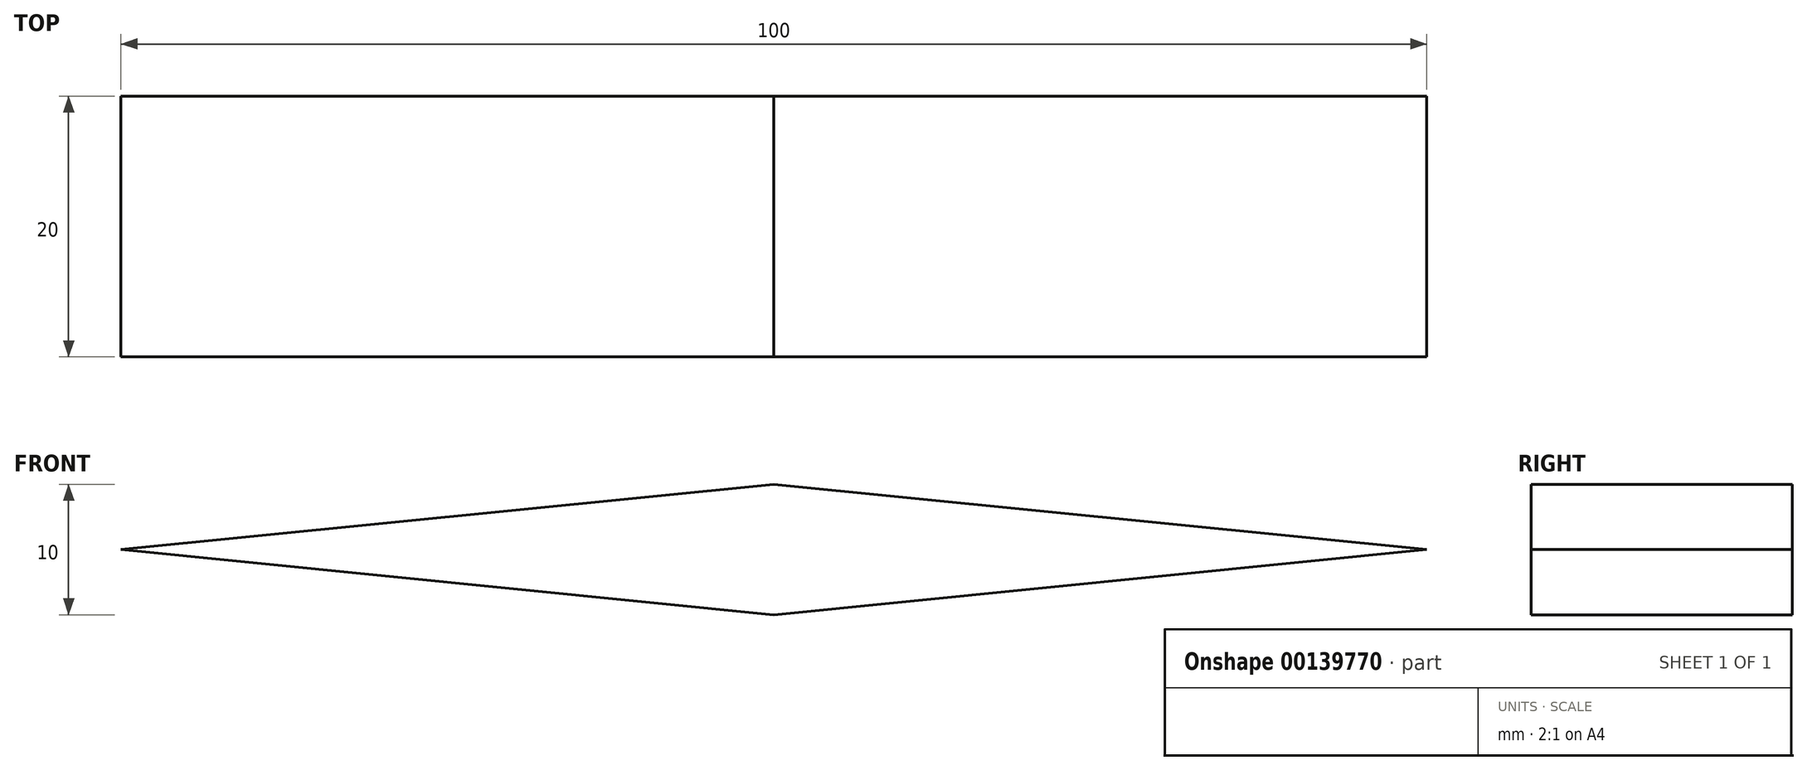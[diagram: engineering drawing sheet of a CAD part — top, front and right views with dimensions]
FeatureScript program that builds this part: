
annotation { "Feature Type Name" : "Feature", "Feature Type Description" : "" }
export const myFeature = defineFeature(function(context is Context, id is Id, definition is map)
    precondition{}
    {
        {
            var Q0;
            Q0=qCreatedBy(makeId("Front.planeOp"),FACE);
            var sketch = newSketch(context, id + "F0", { "sketchPlane" : qUnion([Q0])});
            skLineSegment(sketch, "E0", {"start": v(0, 0) * mm, "end": v(50, 5) * mm});
            skLineSegment(sketch, "E1", {"start": v(50, 5) * mm, "end": v(100, 0) * mm});
            skLineSegment(sketch, "E2", {"start": v(100, 0) * mm, "end": v(50, -5) * mm});
            skLineSegment(sketch, "E3", {"start": v(50, -5) * mm, "end": v(0, 0) * mm});
            skSolve(sketch);
        }
        {
            var Q0;
            Q0 = qSketchRegion(id + "F0", true);
            extrude(context, id + "F1", {"entities" : qUnion([Q0]), "depth" : 20 * mm});
        }
    });
